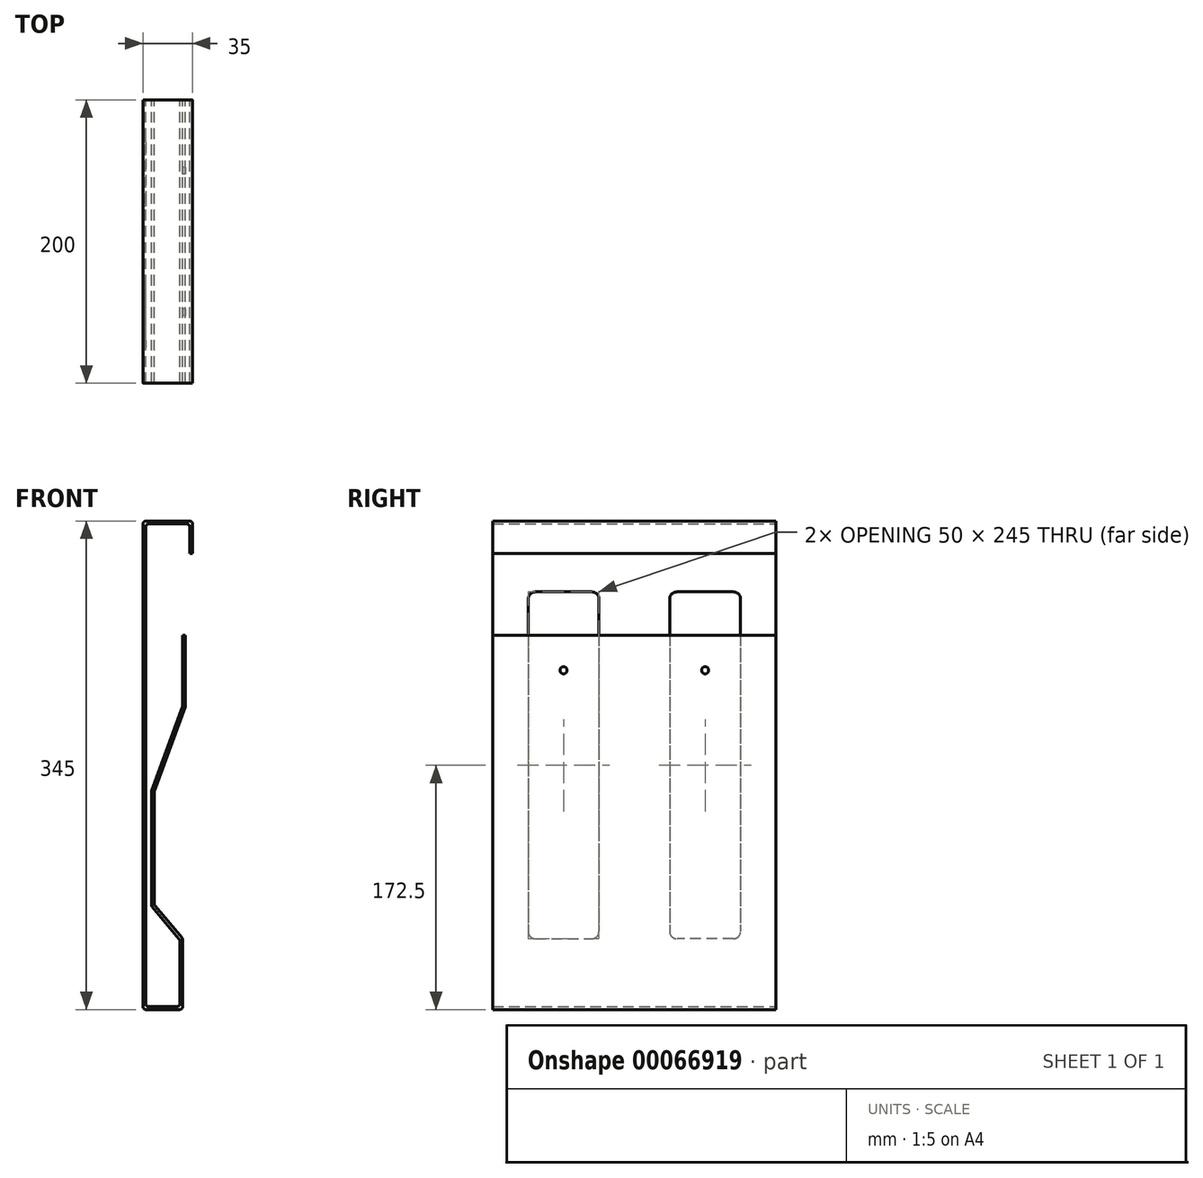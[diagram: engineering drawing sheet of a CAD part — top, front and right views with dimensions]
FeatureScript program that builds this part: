
annotation { "Feature Type Name" : "Feature", "Feature Type Description" : "" }
export const myFeature = defineFeature(function(context is Context, id is Id, definition is map)
    precondition{}
    {
        {
            var Q0;
            Q0=qCreatedBy(makeId("Front.planeOp"),FACE);
            var sketch = newSketch(context, id + "F0", { "sketchPlane" : qUnion([Q0])});
            skLineSegment(sketch, "E0", {"start": v(0, 0) * mm, "end": v(35, 0) * mm});
            skLineSegment(sketch, "E1", {"start": v(35, 0) * mm, "end": v(35, -23) * mm});
            skLineSegment(sketch, "E2", {"start": v(0, 0) * mm, "end": v(0, -345) * mm});
            skLineSegment(sketch, "E3", {"start": v(0, -345) * mm, "end": v(28, -345) * mm});
            skLineSegment(sketch, "E4", {"start": v(28, -295) * mm, "end": v(28, -345) * mm});
            skLineSegment(sketch, "E5.0", {"start": v(33, -2) * mm, "end": v(33, -23) * mm});
            skLineSegment(sketch, "E5.1", {"start": v(26, -295.73) * mm, "end": v(26, -343) * mm});
            skLineSegment(sketch, "E5.2", {"start": v(2, -343) * mm, "end": v(26, -343) * mm});
            skLineSegment(sketch, "E5.3", {"start": v(2, -2) * mm, "end": v(2, -343) * mm});
            skLineSegment(sketch, "E5.4", {"start": v(2, -2) * mm, "end": v(33, -2) * mm});
            skLineSegment(sketch, "E6", {"start": v(33, -23) * mm, "end": v(35, -23) * mm});
            skLineSegment(sketch, "E7", {"start": v(26, -295.73) * mm, "end": v(6, -271.9) * mm});
            skLineSegment(sketch, "E8", {"start": v(6, -271.9) * mm, "end": v(6, -190.81) * mm});
            skLineSegment(sketch, "E9", {"start": v(6, -190.81) * mm, "end": v(28, -130.37) * mm});
            skLineSegment(sketch, "E10", {"start": v(28, -130.37) * mm, "end": v(28, -80.72) * mm});
            skLineSegment(sketch, "E11.0", {"start": v(30, -130.72) * mm, "end": v(30, -80.72) * mm});
            skLineSegment(sketch, "E11.1", {"start": v(8, -191.16) * mm, "end": v(30, -130.72) * mm});
            skLineSegment(sketch, "E11.2", {"start": v(8, -271.16) * mm, "end": v(8, -191.16) * mm});
            skLineSegment(sketch, "E11.3", {"start": v(28, -295) * mm, "end": v(8, -271.16) * mm});
            skLineSegment(sketch, "E12", {"start": v(28, -80.72) * mm, "end": v(30, -80.72) * mm});
            skSolve(sketch);
        }
        {
            var Q0;
            Q0=qSketchRegion(id+"F0",true);
            extrude(context, id + "F1", {"entities" : qUnion([Q0]), "depth" : 200 * mm});
        }
        {
            var Q0;
            Q0=makeQuery(id+"F1.opExtrude","SWEPT_EDGE",EDGE,{"disambiguationData":[OSD([sQuery(id+"F0.wireOp",EDGE,"E0"),sQuery(id+"F0.wireOp",EDGE,"E2")])]});
            var Q1;
            Q1=makeQuery(id+"F1.opExtrude","SWEPT_EDGE",EDGE,{"disambiguationData":[OSD([sQuery(id+"F0.wireOp",EDGE,"E0"),sQuery(id+"F0.wireOp",EDGE,"E1")])]});
            var Q2;
            Q2=makeQuery(id+"F1.opExtrude","SWEPT_EDGE",EDGE,{"disambiguationData":[OSD([sQuery(id+"F0.wireOp",EDGE,"E5.0"),sQuery(id+"F0.wireOp",EDGE,"E5.4")])]});
            var Q3;
            Q3=makeQuery(id+"F1.opExtrude","SWEPT_EDGE",EDGE,{"disambiguationData":[OSD([sQuery(id+"F0.wireOp",EDGE,"E5.3"),sQuery(id+"F0.wireOp",EDGE,"E5.4")])]});
            var Q4;
            Q4=makeQuery(id+"F1.opExtrude","SWEPT_EDGE",EDGE,{"disambiguationData":[OSD([sQuery(id+"F0.wireOp",EDGE,"E2"),sQuery(id+"F0.wireOp",EDGE,"E3")])]});
            var Q5;
            Q5=makeQuery(id+"F1.opExtrude","SWEPT_EDGE",EDGE,{"disambiguationData":[OSD([sQuery(id+"F0.wireOp",EDGE,"E5.2"),sQuery(id+"F0.wireOp",EDGE,"E5.3")])]});
            var Q6;
            Q6=makeQuery(id+"F1.opExtrude","SWEPT_EDGE",EDGE,{"disambiguationData":[OSD([sQuery(id+"F0.wireOp",EDGE,"E3"),sQuery(id+"F0.wireOp",EDGE,"E4")])]});
            var Q7;
            Q7=makeQuery(id+"F1.opExtrude","SWEPT_EDGE",EDGE,{"disambiguationData":[OSD([sQuery(id+"F0.wireOp",EDGE,"E5.1"),sQuery(id+"F0.wireOp",EDGE,"E5.2")])]});
            var Q8;
            Q8=makeQuery(id+"F1.opExtrude","SWEPT_EDGE",EDGE,{"disambiguationData":[OSD([sQuery(id+"F0.wireOp",EDGE,"E5.1"),sQuery(id+"F0.wireOp",EDGE,"E7")])]});
            var Q9;
            Q9=makeQuery(id+"F1.opExtrude","SWEPT_EDGE",EDGE,{"disambiguationData":[OSD([sQuery(id+"F0.wireOp",EDGE,"E4"),sQuery(id+"F0.wireOp",EDGE,"E11.3")])]});
            var Q10;
            Q10=makeQuery(id+"F1.opExtrude","SWEPT_EDGE",EDGE,{"disambiguationData":[OSD([sQuery(id+"F0.wireOp",EDGE,"E11.2"),sQuery(id+"F0.wireOp",EDGE,"E11.3")])]});
            var Q11;
            Q11=makeQuery(id+"F1.opExtrude","SWEPT_EDGE",EDGE,{"disambiguationData":[OSD([sQuery(id+"F0.wireOp",EDGE,"E7"),sQuery(id+"F0.wireOp",EDGE,"E8")])]});
            var Q12;
            Q12=makeQuery(id+"F1.opExtrude","SWEPT_EDGE",EDGE,{"disambiguationData":[OSD([sQuery(id+"F0.wireOp",EDGE,"E8"),sQuery(id+"F0.wireOp",EDGE,"E9")])]});
            var Q13;
            Q13=makeQuery(id+"F1.opExtrude","SWEPT_EDGE",EDGE,{"disambiguationData":[OSD([sQuery(id+"F0.wireOp",EDGE,"E11.1"),sQuery(id+"F0.wireOp",EDGE,"E11.2")])]});
            var Q14;
            Q14=makeQuery(id+"F1.opExtrude","SWEPT_EDGE",EDGE,{"disambiguationData":[OSD([sQuery(id+"F0.wireOp",EDGE,"E11.0"),sQuery(id+"F0.wireOp",EDGE,"E11.1")])]});
            var Q15;
            Q15=makeQuery(id+"F1.opExtrude","SWEPT_EDGE",EDGE,{"disambiguationData":[OSD([sQuery(id+"F0.wireOp",EDGE,"E9"),sQuery(id+"F0.wireOp",EDGE,"E10")])]});
            fillet(context, id + "F2", {"entities" : qUnion([Q0, Q1, Q2, Q3, Q4, Q5, Q6, Q7, Q8, Q9, Q10, Q11, Q12, Q13, Q14, Q15]), "radius" : 2 * mm, "tangentPropagation" : true, "allowEdgeOverflow" : false});
        }
        {
            var Q0;
            Q0=makeQuery(id+"F1.opExtrude","SWEPT_FACE",FACE,{"disambiguationData":[OSD([sQuery(id+"F0.wireOp",EDGE,"E2")])]});
            var sketch = newSketch(context, id + "F3", { "sketchPlane" : qUnion([Q0])});
            skLineSegment(sketch, "E13", {"start": v(100, -2) * mm, "end": v(100, -28.99) * mm, "construction": true});
            skLineSegment(sketch, "E14.bottom", {"start": v(30, -50) * mm, "end": v(70, -50) * mm});
            skLineSegment(sketch, "E14.top", {"start": v(30, -295) * mm, "end": v(70, -295) * mm});
            skLineSegment(sketch, "E14.left", {"start": v(25, -55) * mm, "end": v(25, -290) * mm});
            skLineSegment(sketch, "E14.right", {"start": v(75, -55) * mm, "end": v(75, -290) * mm});
            skPoint(sketch, "E15.visualSharp", {"position": v(25, -50) * mm});
            skArc(sketch, "E15.filletArc", {"start": v(30, -50) * mm, "mid": v(26.46, -51.46) * mm, "end": v(25, -55) * mm});
            skPoint(sketch, "E16.visualSharp", {"position": v(75, -50) * mm});
            skArc(sketch, "E16.filletArc", {"start": v(75, -55) * mm, "mid": v(73.54, -51.46) * mm, "end": v(70, -50) * mm});
            skPoint(sketch, "E17.visualSharp", {"position": v(75, -295) * mm});
            skArc(sketch, "E17.filletArc", {"start": v(70, -295) * mm, "mid": v(73.54, -293.54) * mm, "end": v(75, -290) * mm});
            skPoint(sketch, "E18.visualSharp", {"position": v(25, -295) * mm});
            skArc(sketch, "E18.filletArc", {"start": v(25, -290) * mm, "mid": v(26.46, -293.54) * mm, "end": v(30, -295) * mm});
            skLineSegment(sketch, "E19.MirrorCS", {"start": v(170, -50) * mm, "end": v(130, -50) * mm});
            skArc(sketch, "E20.MirrorCS", {"start": v(175, -290) * mm, "mid": v(173.54, -293.54) * mm, "end": v(170, -295) * mm});
            skArc(sketch, "E21.MirrorCS", {"start": v(130, -295) * mm, "mid": v(126.46, -293.54) * mm, "end": v(125, -290) * mm});
            skLineSegment(sketch, "E22.MirrorCS", {"start": v(170, -295) * mm, "end": v(130, -295) * mm});
            skArc(sketch, "E23.MirrorCS", {"start": v(170, -50) * mm, "mid": v(173.54, -51.46) * mm, "end": v(175, -55) * mm});
            skArc(sketch, "E24.MirrorCS", {"start": v(125, -55) * mm, "mid": v(126.46, -51.46) * mm, "end": v(130, -50) * mm});
            skPoint(sketch, "E25.MirrorP", {"position": v(175, -295) * mm});
            skLineSegment(sketch, "E26.MirrorCS", {"start": v(175, -55) * mm, "end": v(175, -290) * mm});
            skPoint(sketch, "E27.MirrorP", {"position": v(125, -295) * mm});
            skLineSegment(sketch, "E28.MirrorCS", {"start": v(125, -55) * mm, "end": v(125, -290) * mm});
            skPoint(sketch, "E29.MirrorP", {"position": v(125, -50) * mm});
            skPoint(sketch, "E30.MirrorP", {"position": v(175, -50) * mm});
            skSolve(sketch);
        }
        {
            var Q0;
            Q0 = qSketchRegion(id + "F3", true);
            extrude(context, id + "F4", {"entities" : qUnion([Q0]), "operationType" : NewBodyOperationType.REMOVE, "oppositeDirection" : true, "depth" : 2 * mm});
        }
        {
            var Q0;
            Q0=makeQuery(id+"F1.opExtrude","SWEPT_FACE",FACE,{"disambiguationData":[OSD([sQuery(id+"F0.wireOp",EDGE,"E10")])]});
            var sketch = newSketch(context, id + "F5", { "sketchPlane" : qUnion([Q0])});
            skLineSegment(sketch, "E31", {"start": v(0, -105.37) * mm, "end": v(200, -105.37) * mm, "construction": true});
            skPoint(sketch, "E32", {"position": v(50, -105.37) * mm});
            skPoint(sketch, "E33", {"position": v(150, -105.37) * mm});
            skSolve(sketch);
        }
        {
            var Q0;
            Q0=sQuery(id+"F5.wireOp",VERTEX,"E32");
            var Q1;
            Q1=sQuery(id+"F5.wireOp",VERTEX,"E33");
            var Q2;
            Q2=makeQuery(id+"F1.opExtrude","SWEPT_BODY",BODY,{"disambiguationData":[OSD([sQuery(id+"F0.wireOp",EDGE,"E0"),sQuery(id+"F0.wireOp",EDGE,"E1"),sQuery(id+"F0.wireOp",EDGE,"E2"),sQuery(id+"F0.wireOp",EDGE,"E3"),sQuery(id+"F0.wireOp",EDGE,"E4"),sQuery(id+"F0.wireOp",EDGE,"E5.0"),sQuery(id+"F0.wireOp",EDGE,"E5.1"),sQuery(id+"F0.wireOp",EDGE,"E5.2"),sQuery(id+"F0.wireOp",EDGE,"E5.3"),sQuery(id+"F0.wireOp",EDGE,"E5.4"),sQuery(id+"F0.wireOp",EDGE,"E6"),sQuery(id+"F0.wireOp",EDGE,"E7"),sQuery(id+"F0.wireOp",EDGE,"E8"),sQuery(id+"F0.wireOp",EDGE,"E9"),sQuery(id+"F0.wireOp",EDGE,"E10"),sQuery(id+"F0.wireOp",EDGE,"E11.0"),sQuery(id+"F0.wireOp",EDGE,"E11.1"),sQuery(id+"F0.wireOp",EDGE,"E11.2"),sQuery(id+"F0.wireOp",EDGE,"E11.3"),sQuery(id+"F0.wireOp",EDGE,"E12")])]});
            hole(context, id + "F6", {"style" : HoleStyle.SIMPLE, "endStyle" : HoleEndStyle.BLIND, "holeDiameter" : 5 * mm, "holeDepth" : 2 * mm, "locations" : qUnion([Q0, Q1]), "scope" : qUnion([Q2])});
        }
    });
